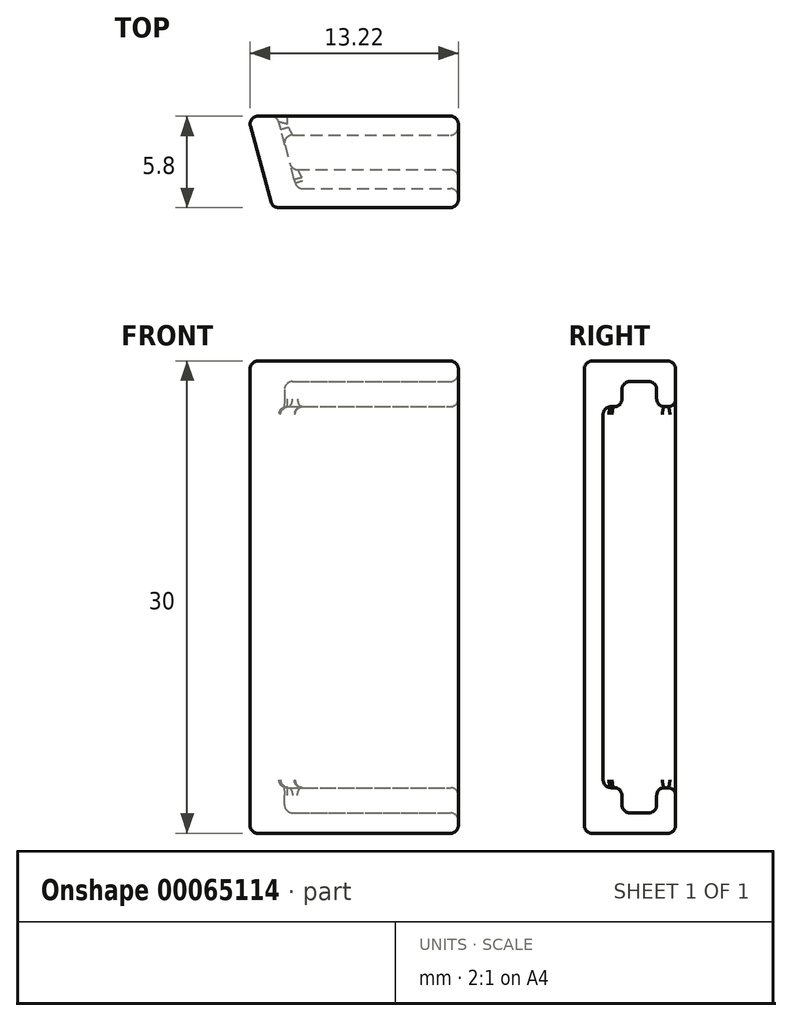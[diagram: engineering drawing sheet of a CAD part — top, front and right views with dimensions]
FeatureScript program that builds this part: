
annotation { "Feature Type Name" : "Feature", "Feature Type Description" : "" }
export const myFeature = defineFeature(function(context is Context, id is Id, definition is map)
    precondition{}
    {
        {
            var Q0;
            Q0=qCreatedBy(makeId("Top.planeOp"),FACE);
            var sketch = newSketch(context, id + "F0", { "sketchPlane" : qUnion([Q0])});
            skLineSegment(sketch, "E0", {"start": v(22.5, 2.5) * mm, "end": v(23.5, 15.5) * mm, "construction": true});
            skLineSegment(sketch, "E1", {"start": v(23.5, 15.5) * mm, "end": v(19, 26) * mm, "construction": true});
            skLineSegment(sketch, "E2", {"start": v(19, 26) * mm, "end": v(25.53, 26) * mm, "construction": true});
            skLineSegment(sketch, "E3", {"start": v(25.53, 26) * mm, "end": v(29.6, 16.5) * mm, "construction": true});
            skLineSegment(sketch, "E4", {"start": v(29.6, 16.5) * mm, "end": v(27.86, -6) * mm, "construction": true});
            skLineSegment(sketch, "E5", {"start": v(27.86, -6) * mm, "end": v(-15.2, -6) * mm, "construction": true});
            skLineSegment(sketch, "E6", {"start": v(-27, -6) * mm, "end": v(-28.58, -0.2) * mm});
            skLineSegment(sketch, "E7", {"start": v(-36.5, 29.01) * mm, "end": v(-36.5, 32) * mm, "construction": true});
            skLineSegment(sketch, "E8", {"start": v(-36.5, 32) * mm, "end": v(-18.5, 32) * mm, "construction": true});
            skLineSegment(sketch, "E9", {"start": v(-18.5, 32) * mm, "end": v(-18.5, 26) * mm, "construction": true});
            skLineSegment(sketch, "E10", {"start": v(-18.5, 26) * mm, "end": v(-23.5, 26) * mm, "construction": true});
            skLineSegment(sketch, "E11", {"start": v(-23.5, 26) * mm, "end": v(-26.7, 15.8) * mm, "construction": true});
            skLineSegment(sketch, "E12", {"start": v(-26.7, 15.8) * mm, "end": v(-23.5, 4) * mm, "construction": true});
            skLineSegment(sketch, "E13", {"start": v(-23.5, 4) * mm, "end": v(-19.5, 0) * mm, "construction": true});
            skLineSegment(sketch, "E14", {"start": v(-19.5, 0) * mm, "end": v(-15.2, 0) * mm, "construction": true});
            skLineSegment(sketch, "E15", {"start": v(19.5, 0) * mm, "end": v(22.5, 2.5) * mm, "construction": true});
            skLineSegment(sketch, "E16", {"start": v(-19.5, 0) * mm, "end": v(-28.63, 0) * mm, "construction": true});
            skLineSegment(sketch, "E17", {"start": v(-15.2, 0) * mm, "end": v(-15.2, -0.2) * mm, "construction": true});
            skLineSegment(sketch, "E18", {"start": v(-15.2, 0) * mm, "end": v(19.5, 0) * mm, "construction": true});
            skLineSegment(sketch, "E19", {"start": v(-15.2, -6) * mm, "end": v(-27, -6) * mm});
            skLineSegment(sketch, "E20", {"start": v(-28.63, 0) * mm, "end": v(-36.5, 29.01) * mm, "construction": true});
            skLineSegment(sketch, "E21", {"start": v(-28.58, -0.2) * mm, "end": v(-15.2, -0.2) * mm});
            skLineSegment(sketch, "E22", {"start": v(-28.58, -0.2) * mm, "end": v(-28.63, 0) * mm, "construction": true});
            skLineSegment(sketch, "E23", {"start": v(-15.2, -0.2) * mm, "end": v(-15.2, -6) * mm});
            skSolve(sketch);
        }
        {
            var Q0;
            Q0=qSketchRegion(id+"F0",true);
            extrude(context, id + "F1", {"entities" : qUnion([Q0]), "depth" : 15 * mm});
        }
        {
            var Q0;
            Q0=qCreatedBy(makeId("Top.planeOp"),FACE);
            var sketch = newSketch(context, id + "F2", { "sketchPlane" : qUnion([Q0])});
            skLineSegment(sketch, "E24.0", {"start": v(19.86, 24) * mm, "end": v(19, 26) * mm});
            skLineSegment(sketch, "E25.0", {"start": v(19, 26) * mm, "end": v(25.53, 26) * mm});
            skLineSegment(sketch, "E26.0", {"start": v(25.53, 26) * mm, "end": v(29.6, 16.5) * mm});
            skLineSegment(sketch, "E27", {"start": v(19.86, 24) * mm, "end": v(24.86, 24) * mm});
            skLineSegment(sketch, "E28", {"start": v(24.86, 24) * mm, "end": v(28.17, 16.27) * mm});
            skLineSegment(sketch, "E29", {"start": v(28.17, 16.27) * mm, "end": v(29.6, 16.5) * mm});
            skPoint(sketch, "E30.orphan", {"position": v(23.5, 15.5) * mm});
            skLineSegment(sketch, "E31.0", {"start": v(-27, -6) * mm, "end": v(-28.63, 0) * mm, "construction": true});
            skLineSegment(sketch, "E32.0", {"start": v(-15, -6) * mm, "end": v(-15.2, -6) * mm, "construction": true});
            skLineSegment(sketch, "E33", {"start": v(-28.63, 0) * mm, "end": v(-26.77, 0) * mm, "construction": true});
            skLineSegment(sketch, "E34", {"start": v(-26.77, 0) * mm, "end": v(-25.47, -4.8) * mm});
            skLineSegment(sketch, "E35", {"start": v(-25.47, -4.8) * mm, "end": v(-15, -4.8) * mm});
            skLineSegment(sketch, "E36", {"start": v(-15, -4.8) * mm, "end": v(-15, -6) * mm, "construction": true});
            skPoint(sketch, "E37.orphan", {"position": v(27.86, -6) * mm});
            skPoint(sketch, "E38.orphan", {"position": v(-28.58, -0.2) * mm});
            skLineSegment(sketch, "E39", {"start": v(-26.77, 0) * mm, "end": v(-15, 0) * mm});
            skLineSegment(sketch, "E40", {"start": v(-15, 0) * mm, "end": v(-15, -4.8) * mm});
            skSolve(sketch);
        }
        {
            var Q0;
            Q0=qCreatedBy(makeId("Top.planeOp"),FACE);
            var sketch = newSketch(context, id + "F3", { "sketchPlane" : qUnion([Q0])});
            skLineSegment(sketch, "E41", {"start": v(22.72, 20.88) * mm, "end": v(24.74, 21.75) * mm});
            skLineSegment(sketch, "E42", {"start": v(24.74, 21.75) * mm, "end": v(26.79, 16.97) * mm});
            skLineSegment(sketch, "E43", {"start": v(26.79, 16.97) * mm, "end": v(24.77, 16.1) * mm});
            skLineSegment(sketch, "E44", {"start": v(24.77, 16.1) * mm, "end": v(22.72, 20.88) * mm});
            skLineSegment(sketch, "E45", {"start": v(-23.4, -1.4) * mm, "end": v(-18.2, -1.4) * mm});
            skLineSegment(sketch, "E46", {"start": v(-18.2, -1.4) * mm, "end": v(-18.2, -3.6) * mm, "construction": true});
            skLineSegment(sketch, "E47", {"start": v(-18.2, -3.6) * mm, "end": v(-23.4, -3.6) * mm});
            skLineSegment(sketch, "E48", {"start": v(-23.4, -3.6) * mm, "end": v(-23.4, -1.4) * mm, "construction": true});
            skLineSegment(sketch, "E49", {"start": v(-33.35, 26.55) * mm, "end": v(-31.22, 27.13) * mm});
            skLineSegment(sketch, "E50", {"start": v(-31.22, 27.13) * mm, "end": v(-29.86, 22.11) * mm});
            skLineSegment(sketch, "E51", {"start": v(-29.86, 22.11) * mm, "end": v(-31.99, 21.53) * mm});
            skLineSegment(sketch, "E52", {"start": v(-31.99, 21.53) * mm, "end": v(-33.35, 26.55) * mm});
            skLineSegment(sketch, "E53", {"start": v(-32.28, 26.84) * mm, "end": v(-30.92, 21.82) * mm, "construction": true});
            skLineSegment(sketch, "E54", {"start": v(-23.4, -2.5) * mm, "end": v(-18.2, -2.5) * mm, "construction": true});
            skLineSegment(sketch, "E55", {"start": v(25.78, 16.53) * mm, "end": v(23.73, 21.31) * mm, "construction": true});
            skLineSegment(sketch, "E56", {"start": v(-23.4, -3.6) * mm, "end": v(-27, -6) * mm, "construction": true});
            skLineSegment(sketch, "E57", {"start": v(-33.35, 26.55) * mm, "end": v(-36.5, 29.01) * mm, "construction": true});
            skLineSegment(sketch, "E58", {"start": v(24.74, 21.75) * mm, "end": v(25.53, 26) * mm, "construction": true});
            skLineSegment(sketch, "E59", {"start": v(-23.4, -1.4) * mm, "end": v(-26.39, -1.4) * mm});
            skLineSegment(sketch, "E60", {"start": v(-26.39, -1.4) * mm, "end": v(-25.8, -3.6) * mm});
            skLineSegment(sketch, "E61", {"start": v(-25.8, -3.6) * mm, "end": v(-23.4, -3.6) * mm});
            skLineSegment(sketch, "E62", {"start": v(-18.2, -1.4) * mm, "end": v(-15, -1.4) * mm});
            skLineSegment(sketch, "E63", {"start": v(-15, -1.4) * mm, "end": v(-15, -3.6) * mm});
            skLineSegment(sketch, "E64", {"start": v(-15, -3.6) * mm, "end": v(-18.2, -3.6) * mm});
            skSolve(sketch);
        }
        {
            var Q0;
            Q0 = qSketchRegion(id + "F3", true);
            extrude(context, id + "F4", {"entities" : qUnion([Q0]), "operationType" : NewBodyOperationType.REMOVE, "depth" : 13.7 * mm});
        }
        {
            var Q0;
            Q0 = qSketchRegion(id + "F2", true);
            extrude(context, id + "F5", {"entities" : qUnion([Q0]), "operationType" : NewBodyOperationType.REMOVE, "depth" : 12.1 * mm});
        }
        {
            var Q0;
            Q0=makeQuery(id+"F4.boolean.opBoolean","COPY",EDGE,{"derivedFrom":makeQuery(id+"F4.opExtrude","CAP_EDGE",EDGE,{"disambiguationData":[OSD([sQuery(id+"F3.wireOp",EDGE,"E45"),sQuery(id+"F3.wireOp",EDGE,"E59"),sQuery(id+"F3.wireOp",EDGE,"E62")])],"isStart":false})});
            var Q1;
            Q1=makeQuery(id+"F5.boolean.opBoolean","INTERSECT",EDGE,{"derivedFrom":[makeQuery(id+"F4.boolean.opBoolean","COPY",FACE,{"derivedFrom":makeQuery(id+"F4.opExtrude","SWEPT_FACE",FACE,{"disambiguationData":[OSD([sQuery(id+"F3.wireOp",EDGE,"E45"),sQuery(id+"F3.wireOp",EDGE,"E59"),sQuery(id+"F3.wireOp",EDGE,"E62")])]})}),makeQuery(id+"F5.opExtrude","CAP_FACE",FACE,{"disambiguationData":[OSD([sQuery(id+"F2.wireOp",EDGE,"E34"),sQuery(id+"F2.wireOp",EDGE,"E35"),sQuery(id+"F2.wireOp",EDGE,"E39"),sQuery(id+"F2.wireOp",EDGE,"E40")])],"isStart":false})]});
            var Q2;
            Q2=makeQuery(id+"F5.boolean.opBoolean","COPY",EDGE,{"disambiguationData":[OD(1.0)],"derivedFrom":makeQuery(id+"F5.opExtrude","CAP_EDGE",EDGE,{"disambiguationData":[OSD([sQuery(id+"F2.wireOp",EDGE,"E34")])],"isStart":false})});
            var Q3;
            Q3=makeQuery(id+"F5.boolean.opBoolean","COPY",EDGE,{"derivedFrom":makeQuery(id+"F5.opExtrude","SWEPT_EDGE",EDGE,{"disambiguationData":[OSD([sQuery(id+"F2.wireOp",EDGE,"E34"),sQuery(id+"F2.wireOp",EDGE,"E35")])]})});
            var Q4;
            Q4=makeQuery(id+"F5.boolean.opBoolean","COPY",EDGE,{"disambiguationData":[OD(0.0)],"derivedFrom":makeQuery(id+"F5.opExtrude","CAP_EDGE",EDGE,{"disambiguationData":[OSD([sQuery(id+"F2.wireOp",EDGE,"E34")])],"isStart":false})});
            var Q5;
            Q5=makeQuery(id+"F4.boolean.opBoolean","COPY",EDGE,{"derivedFrom":makeQuery(id+"F4.opExtrude","SWEPT_EDGE",EDGE,{"disambiguationData":[OSD([sQuery(id+"F3.wireOp",EDGE,"E60"),sQuery(id+"F3.wireOp",EDGE,"E61")])]})});
            var Q6;
            Q6=makeQuery(id+"F5.boolean.opBoolean","INTERSECT",EDGE,{"derivedFrom":[makeQuery(id+"F4.boolean.opBoolean","COPY",FACE,{"derivedFrom":makeQuery(id+"F4.opExtrude","SWEPT_FACE",FACE,{"disambiguationData":[OSD([sQuery(id+"F3.wireOp",EDGE,"E47"),sQuery(id+"F3.wireOp",EDGE,"E61"),sQuery(id+"F3.wireOp",EDGE,"E64")])]})}),makeQuery(id+"F5.opExtrude","CAP_FACE",FACE,{"disambiguationData":[OSD([sQuery(id+"F2.wireOp",EDGE,"E34"),sQuery(id+"F2.wireOp",EDGE,"E35"),sQuery(id+"F2.wireOp",EDGE,"E39"),sQuery(id+"F2.wireOp",EDGE,"E40")])],"isStart":false})]});
            var Q7;
            Q7=makeQuery(id+"F5.boolean.opBoolean","COPY",EDGE,{"derivedFrom":makeQuery(id+"F5.opExtrude","CAP_EDGE",EDGE,{"disambiguationData":[OSD([sQuery(id+"F2.wireOp",EDGE,"E35")])],"isStart":false})});
            var Q8;
            Q8=makeQuery(id+"F4.boolean.opBoolean","COPY",EDGE,{"derivedFrom":makeQuery(id+"F4.opExtrude","CAP_EDGE",EDGE,{"disambiguationData":[OSD([sQuery(id+"F3.wireOp",EDGE,"E47"),sQuery(id+"F3.wireOp",EDGE,"E61"),sQuery(id+"F3.wireOp",EDGE,"E64")])],"isStart":false})});
            var Q9;
            Q9=makeQuery(id+"F4.boolean.opBoolean","COPY",EDGE,{"derivedFrom":makeQuery(id+"F4.opExtrude","CAP_EDGE",EDGE,{"disambiguationData":[OSD([sQuery(id+"F3.wireOp",EDGE,"E60")])],"isStart":false})});
            var Q10;
            Q10=makeQuery(id+"F4.boolean.opBoolean","COPY",EDGE,{"derivedFrom":makeQuery(id+"F4.opExtrude","SWEPT_EDGE",EDGE,{"disambiguationData":[OSD([sQuery(id+"F3.wireOp",EDGE,"E59"),sQuery(id+"F3.wireOp",EDGE,"E60")])]})});
            fillet(context, id + "F6", {"entities" : qUnion([Q0, Q1, Q2, Q3, Q4, Q5, Q6, Q7, Q8, Q9, Q10]), "radius" : .5 * mm, "tangentPropagation" : true, "allowEdgeOverflow" : false});
        }
        {
            var Q0;
            Q0=makeQuery(id+"F1.opExtrude","SWEPT_BODY",BODY,{"disambiguationData":[OSD([sQuery(id+"F0.wireOp",EDGE,"E6"),sQuery(id+"F0.wireOp",EDGE,"E19"),sQuery(id+"F0.wireOp",EDGE,"E21"),sQuery(id+"F0.wireOp",EDGE,"E23")])]});
            var Q1;
            Q1=qCreatedBy(makeId("Top.planeOp"),FACE);
            mirror(context, id + "F7", {"operationType" : NewBodyOperationType.ADD, "entities" : qUnion([Q0]), "mirrorPlane" : qUnion([Q1])});
        }
        {
            var Q0;
            {var subQ0=makeQuery(id+"F1.opExtrude","SWEPT_FACE",FACE,{"disambiguationData":[OSD([sQuery(id+"F0.wireOp",EDGE,"E21")])]});Q0=makeQuery(id+"F7.boolean.opBoolean","MERGE",FACE,{"derivedFrom":[subQ0,makeQuery(id+"F7.opPattern","COPY",FACE,{"derivedFrom":subQ0,"instanceName":"1"})]});}
            var Q1;
            {var subQ0=makeQuery(id+"F1.opExtrude","SWEPT_FACE",FACE,{"disambiguationData":[OSD([sQuery(id+"F0.wireOp",EDGE,"E23")])]});Q1=makeQuery(id+"F7.boolean.opBoolean","MERGE",FACE,{"derivedFrom":[subQ0,makeQuery(id+"F7.opPattern","COPY",FACE,{"derivedFrom":subQ0,"instanceName":"1"})]});}
            var Q2;
            {var subQ0=makeQuery(id+"F1.opExtrude","SWEPT_FACE",FACE,{"disambiguationData":[OSD([sQuery(id+"F0.wireOp",EDGE,"E19")])]});Q2=makeQuery(id+"F7.boolean.opBoolean","MERGE",FACE,{"derivedFrom":[subQ0,makeQuery(id+"F7.opPattern","COPY",FACE,{"derivedFrom":subQ0,"instanceName":"1"})]});}
            var Q3;
            {var subQ0=makeQuery(id+"F1.opExtrude","SWEPT_FACE",FACE,{"disambiguationData":[OSD([sQuery(id+"F0.wireOp",EDGE,"E6")])]});Q3=makeQuery(id+"F7.boolean.opBoolean","MERGE",FACE,{"derivedFrom":[subQ0,makeQuery(id+"F7.opPattern","COPY",FACE,{"derivedFrom":subQ0,"instanceName":"1"})]});}
            fillet(context, id + "F8", {"entities" : qUnion([Q0, Q1, Q2, Q3]), "radius" : .5 * mm, "tangentPropagation" : true, "allowEdgeOverflow" : false});
        }
    });
